# Revit family: NBS_DudleyIndustriesLimited_PprTwlDpnsrs_ModuloAutoCutTowelDispenser
name_source: partatom
category: Electrical Equipment
revit_build: Autodesk Revit 2017 (Build: 20171027_0315(x64)
units: mm (PartAtom-declared; Revit-internal decimal feet)

## family parameters
Always vertical = Yes
Cut with Voids When Loaded = No
Panel Configuration = Two Columns, Circuits Across
Part Type = Panelboard
Room Calculation Point = No
Round Connector Dimension = Use Diameter
Shared = No
Work Plane-Based = No

## types (1)
- ModuloAutoCutTowelDispenser
    AssetType = Fixed
    AutoCutBodyMaterial = NBS_Concept
    BIMObjectName = NBS_DudleyIndustriesLimited_PaperTowelDispensers_ModuloAutoCutTowelDispenser
    Category = Pr_40_70_22_62:Paper towel dispensers
    Color = Black
    Description = Autocut paper towel dispenser provides a hygienic hand drying solution, the dispenser detects the movement of a hand underneath and dispenses a portion of new paper towel and automatically cuts it
    DispensingLength = 190 mm, 280 mm, 370 mm
    DurationUnit = year
    ExpectedLife = 5
    Features = fits the modulo behind the mirror system, provides a hygienic solution as user only touches the paper towel dispensed, no need to touch the unit helping to reduce cleaning requirements, option to have short piece of paper towel visible for next user or none, 3 options for length of towel dispensed: 19cm, 28cm or 37cm, 3 options for sensor range from 3cm to 8cm, consumables not accessible and kept free from contamination by lockable cabinet cover, quick and easy to refill, spare consumables can be conveniently stored, on the shelf within the cabinet, requires 4 x D Cell Batteries, utilises a full modular cabinet space, blanking plates available separately if required
    Finish = Matte black powder coated
    Form = Fits the modulo behind the mirror system
    Grade = Stainless steel, EN1.4509
    HasProtectiveEarth = No
    IfcExportAs = IfcFurnitureType
    IfcExportType = NOTDEFINED
    IsBuiltIn = Yes
    ManufacturerName = Dudley Industries Limited
    ManufacturerURL = https://www.dudleyindustries.com
    Material = Stainless steel
    MaterialsBody = Stainless steel frame, plastic mechanism
    MaterialsFinishAndColour = Matte black powder coated
    ModelNumber = 92371BK
    ModelReference = Modulo Auto Cut Towel Dispenser
    NBSCertification = www.nationalbimlibrary.com/cert/vpve400d
    NBSDescription = Paper towel dispensers
    NBSReference = 45-35-72/344
    Name = PaperTowelDispensers_ModuloAutoCutTowelDispenser_DudleyIndustriesLimited
    NominalDepth = 193 mm
    NominalHeight = 415 mm
    NominalLength = 388 mm  [stored 1.27297 ft]
    NominalWidth = 388 mm  [stored 1.27297 ft]
    NumberOfPoles = 0
    Operation = No Touch
    PowerFactor = 0
    RatedCurrent = 1200mA
    RatedVoltage = 6v dc
    Size = 388 x 415 x 193 mm
    Status = New
    Style = Paper towel dispensers
    TowelsTowelType = Paper
    TowelsWidth = 195 / 210 mm
    Uniclass2015Code = Pr_40_70_22_62
    Uniclass2015Title = Paper towel dispensers
    Uniclass2015Version = Products v1.12
    Version = 1
    WarrantyDurationUnit = 5 year
    Weight = 3.5 kg

note: [stored X ft] marks values corroborated as IEEE doubles in the binary element streams (Revit-internal decimal feet)

## geometry (parser evidence)
native form markers: Sweep x2
no freeform markers — native parametric forms only
